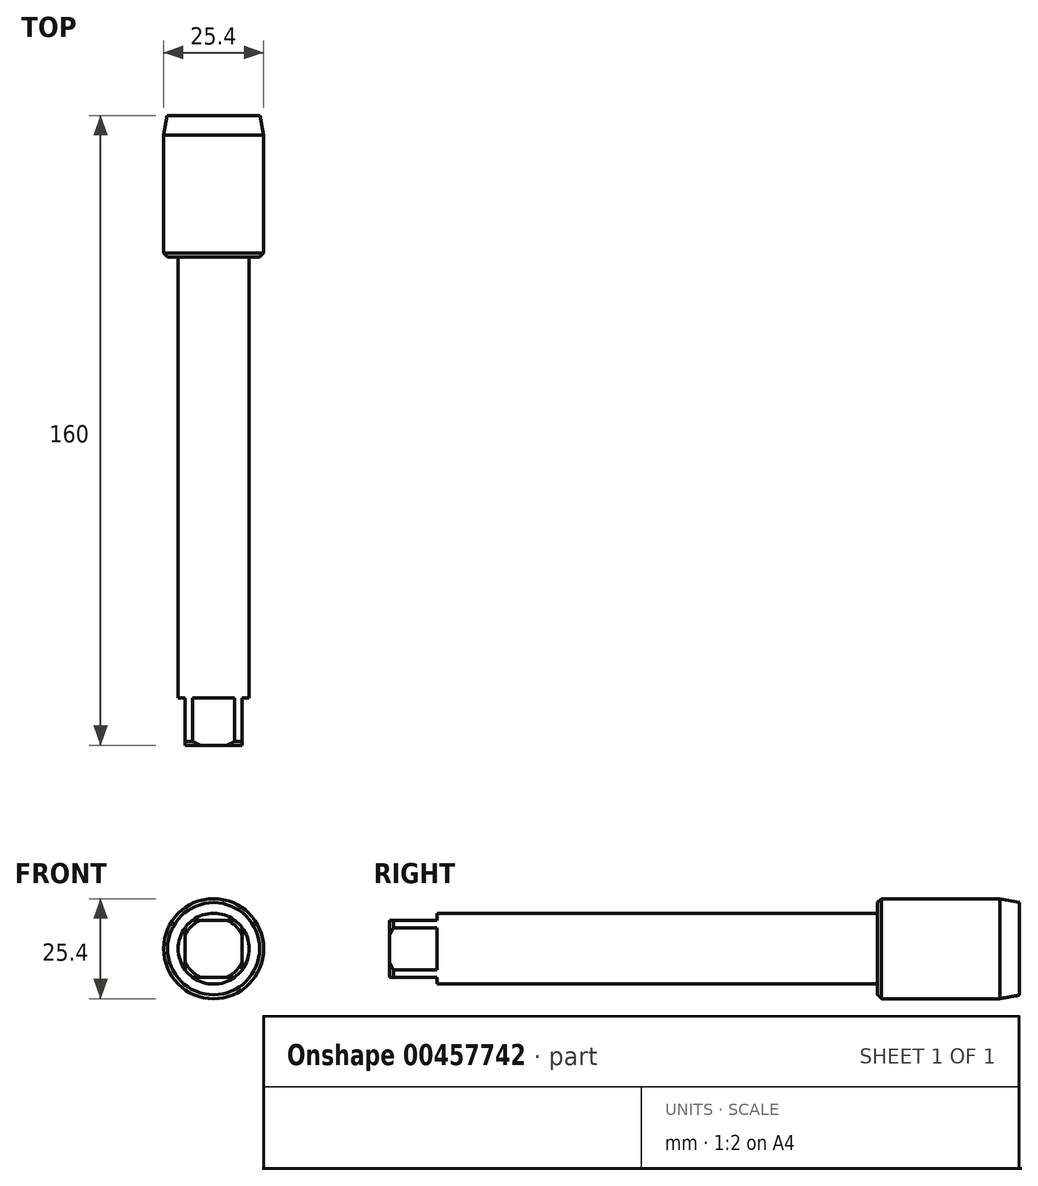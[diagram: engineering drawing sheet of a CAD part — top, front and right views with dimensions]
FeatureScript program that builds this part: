
annotation { "Feature Type Name" : "Feature", "Feature Type Description" : "" }
export const myFeature = defineFeature(function(context is Context, id is Id, definition is map)
    precondition{}
    {
        {
            var Q0;
            Q0=qCreatedBy(makeId("Front.planeOp"),FACE);
            var sketch = newSketch(context, id + "F0", { "sketchPlane" : qUnion([Q0])});
            skCircle(sketch, "E0", {"center": v(0, 0) * mm, "radius": 9 * mm});
            skSolve(sketch);
        }
        {
            var Q0;
            Q0=makeQuery(id+"F0.imprint","IMPRINT",FACE,{"disambiguationData":[TD([[makeQuery(id+"F0.imprint","IMPRINT",EDGE,{"derivedFrom":sQuery(id+"F0.wireOp",EDGE,"E0")}),1.0]])]});
            extrude(context, id + "F1", {"entities" : qUnion([Q0]), "depth" : 160 * mm});
        }
        {
            var Q0;
            Q0=qCreatedBy(makeId("Front.planeOp"),FACE);
            var sketch = newSketch(context, id + "F2", { "sketchPlane" : qUnion([Q0])});
            skCircle(sketch, "E1", {"center": v(0, 0) * mm, "radius": 12.7 * mm});
            skSolve(sketch);
        }
        {
            var Q0;
            Q0 = qSketchRegion(id + "F2", true);
            extrude(context, id + "F3", {"entities" : qUnion([Q0]), "operationType" : NewBodyOperationType.ADD, "depth" : 36 * mm});
        }
        {
            var Q0;
            Q0=makeQuery(id+"F3.opExtrude","CAP_EDGE",EDGE,{"disambiguationData":[OSD([sQuery(id+"F2.wireOp",EDGE,"E1")])],"isStart":true});
            chamfer(context, id + "F4", {"entities" : qUnion([Q0]), "chamferType" : ChamferType.OFFSET_ANGLE, "width" : 5 * mm, "oppositeDirection" : false, "angle" : 10 * degree, "tangentPropagation" : true});
        }
        {
            var Q0;
            Q0=makeQuery(id+"F3.opExtrude","CAP_EDGE",EDGE,{"disambiguationData":[OSD([sQuery(id+"F2.wireOp",EDGE,"E1")])],"isStart":false});
            var Q1;
            Q1=makeQuery(id+"F1.opExtrude","CAP_FACE",FACE,{"disambiguationData":[OSD([sQuery(id+"F0.wireOp",EDGE,"E0")])],"isStart":false});
            chamfer(context, id + "F5", {"entities" : qUnion([Q0, Q1]), "width" : 1 * mm, "tangentPropagation" : true});
        }
        {
            var Q0;
            Q0=makeQuery(id+"F1.opExtrude","CAP_FACE",FACE,{"disambiguationData":[OSD([sQuery(id+"F0.wireOp",EDGE,"E0")])],"isStart":false});
            var sketch = newSketch(context, id + "F6", { "sketchPlane" : qUnion([Q0])});
            skLineSegment(sketch, "E2.bottom", {"start": v(-9.48, -11.15) * mm, "end": v(9.48, -11.15) * mm});
            skLineSegment(sketch, "E2.top", {"start": v(-9.48, 9.84) * mm, "end": v(9.48, 9.84) * mm});
            skLineSegment(sketch, "E2.left", {"start": v(-9.48, -11.15) * mm, "end": v(-9.48, 9.84) * mm});
            skLineSegment(sketch, "E2.right", {"start": v(9.48, -11.15) * mm, "end": v(9.48, 9.84) * mm});
            skPoint(sketch, "E2.middle", {"position": v(0, -0.66) * mm});
            skLineSegment(sketch, "E3.bottom", {"start": v(-7.25, -7.25) * mm, "end": v(7.25, -7.25) * mm});
            skLineSegment(sketch, "E3.top", {"start": v(-7.25, 7.25) * mm, "end": v(7.25, 7.25) * mm});
            skLineSegment(sketch, "E3.left", {"start": v(-7.25, -7.25) * mm, "end": v(-7.25, 7.25) * mm});
            skLineSegment(sketch, "E3.right", {"start": v(7.25, -7.25) * mm, "end": v(7.25, 7.25) * mm});
            skPoint(sketch, "E3.middle", {"position": v(0, 0) * mm});
            skSolve(sketch);
        }
        {
            var Q0;
            Q0 = qSketchRegion(id + "F6", true);
            extrude(context, id + "F7", {"entities" : qUnion([Q0]), "operationType" : NewBodyOperationType.REMOVE, "oppositeDirection" : true, "depth" : 12 * mm});
        }
    });
